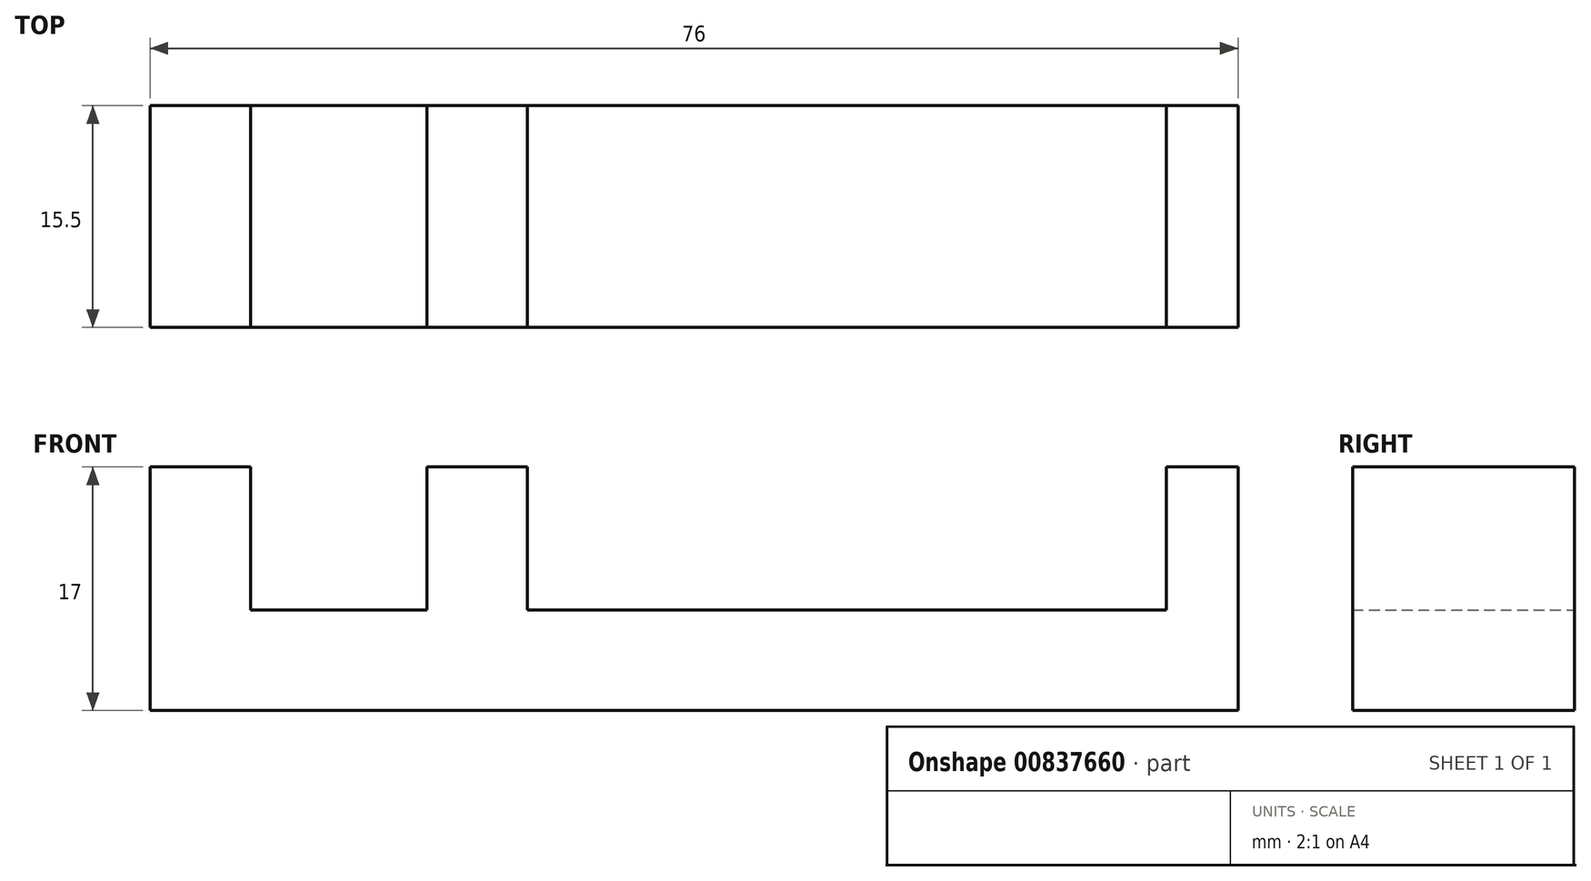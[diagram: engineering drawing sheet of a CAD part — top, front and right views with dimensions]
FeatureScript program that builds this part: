
annotation { "Feature Type Name" : "Feature", "Feature Type Description" : "" }
export const myFeature = defineFeature(function(context is Context, id is Id, definition is map)
    precondition{}
    {
        {
            var Q0;
            Q0=qCreatedBy(makeId("Top.planeOp"),FACE);
            var sketch = newSketch(context, id + "F0", { "sketchPlane" : qUnion([Q0])});
            skLineSegment(sketch, "E0.bottom", {"start": v(-22.83, -7.75) * mm, "end": v(-91.83, -7.75) * mm});
            skLineSegment(sketch, "E0.top", {"start": v(-22.83, 7.75) * mm, "end": v(-91.83, 7.75) * mm});
            skLineSegment(sketch, "E0.left", {"start": v(-22.83, -7.75) * mm, "end": v(-22.83, 7.75) * mm});
            skLineSegment(sketch, "E0.right", {"start": v(-91.83, -7.75) * mm, "end": v(-91.83, 7.75) * mm});
            skPoint(sketch, "E0.middle", {"position": v(-57.33, 0) * mm});
            skLineSegment(sketch, "E1.bottom", {"start": v(-98.83, 7.75) * mm, "end": v(-91.83, 7.75) * mm});
            skLineSegment(sketch, "E1.top", {"start": v(-98.83, -7.75) * mm, "end": v(-91.83, -7.75) * mm});
            skLineSegment(sketch, "E1.left", {"start": v(-91.83, 7.75) * mm, "end": v(-91.83, -7.75) * mm});
            skLineSegment(sketch, "E1.right", {"start": v(-98.83, 7.75) * mm, "end": v(-98.83, -7.75) * mm});
            skLineSegment(sketch, "E2.bottom", {"start": v(-79.49, 7.75) * mm, "end": v(-72.49, 7.75) * mm});
            skLineSegment(sketch, "E2.top", {"start": v(-79.49, -7.75) * mm, "end": v(-72.49, -7.75) * mm});
            skLineSegment(sketch, "E2.left", {"start": v(-79.49, 7.75) * mm, "end": v(-79.49, -7.75) * mm});
            skLineSegment(sketch, "E2.right", {"start": v(-72.49, 7.75) * mm, "end": v(-72.49, -7.75) * mm});
            skLineSegment(sketch, "E3", {"start": v(-27.83, 7.75) * mm, "end": v(-27.83, -7.75) * mm});
            skSolve(sketch);
        }
        {
            var Q0;
            Q0=makeQuery(id+"F0.imprint","IMPRINT",FACE,{"disambiguationData":[TD([[makeQuery(id+"F0.imprint","IMPRINT",EDGE,{"derivedFrom":sQuery(id+"F0.wireOp",EDGE,"E0.right")}),1.0]])]});
            var Q1;
            {var subQ0=sQuery(id+"F0.wireOp",EDGE,"E0.right");Q1=makeQuery(id+"F0.imprint","IMPRINT",FACE,{"disambiguationData":[TD([[makeQuery(id+"F0.imprint","IMPRINT",EDGE,{"derivedFrom":subQ0}),-1.0]])]});}
            var Q2;
            {var subQ0=sQuery(id+"F0.wireOp",EDGE,"E2.left");Q2=makeQuery(id+"F0.imprint","IMPRINT",FACE,{"disambiguationData":[TD([[makeQuery(id+"F0.imprint","IMPRINT",EDGE,{"derivedFrom":subQ0}),1.0]])]});}
            var Q3;
            {var subQ2=sQuery(id+"F0.wireOp",EDGE,"E2.right");Q3=makeQuery(id+"F0.imprint","IMPRINT",FACE,{"disambiguationData":[TD([[makeQuery(id+"F0.imprint","IMPRINT",EDGE,{"derivedFrom":subQ2}),1.0]])]});}
            var Q4;
            {var subQ2=sQuery(id+"F0.wireOp",EDGE,"E0.left");Q4=makeQuery(id+"F0.imprint","IMPRINT",FACE,{"disambiguationData":[TD([[makeQuery(id+"F0.imprint","IMPRINT",EDGE,{"derivedFrom":subQ2}),1.0]])]});}
            extrude(context, id + "F1", {"entities" : qUnion([Q0, Q1, Q2, Q3, Q4]), "depth" : 7 * mm, "offsetDistance" : 25 * mm});
        }
        {
            var Q0;
            Q0=makeQuery(id+"F0.imprint","IMPRINT",FACE,{"disambiguationData":[TD([[makeQuery(id+"F0.imprint","IMPRINT",EDGE,{"derivedFrom":sQuery(id+"F0.wireOp",EDGE,"E0.right")}),1.0]])]});
            var Q1;
            {var subQ0=sQuery(id+"F0.wireOp",EDGE,"E2.left");Q1=makeQuery(id+"F0.imprint","IMPRINT",FACE,{"disambiguationData":[TD([[makeQuery(id+"F0.imprint","IMPRINT",EDGE,{"derivedFrom":subQ0}),1.0]])]});}
            var Q2;
            {var subQ2=sQuery(id+"F0.wireOp",EDGE,"E0.left");Q2=makeQuery(id+"F0.imprint","IMPRINT",FACE,{"disambiguationData":[TD([[makeQuery(id+"F0.imprint","IMPRINT",EDGE,{"derivedFrom":subQ2}),1.0]])]});}
            extrude(context, id + "F2", {"entities" : qUnion([Q0, Q1, Q2]), "operationType" : NewBodyOperationType.ADD, "depth" : 17 * mm, "offsetDistance" : 25 * mm});
        }
    });
